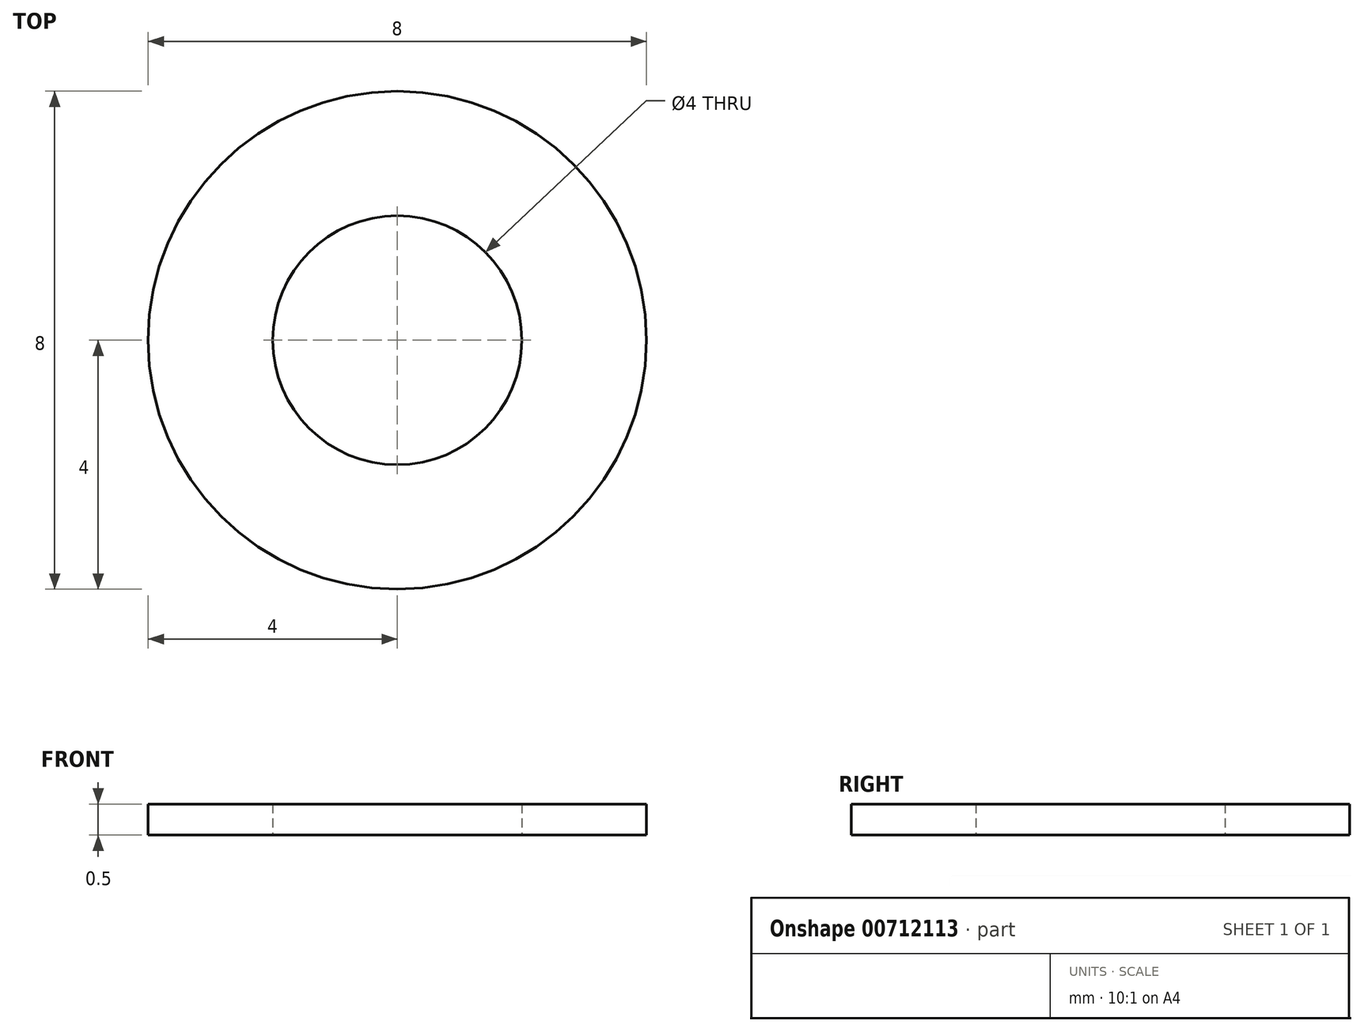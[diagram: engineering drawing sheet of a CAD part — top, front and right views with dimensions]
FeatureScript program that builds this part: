
annotation { "Feature Type Name" : "Feature", "Feature Type Description" : "" }
export const myFeature = defineFeature(function(context is Context, id is Id, definition is map)
    precondition{}
    {
        {
            var Q0;
            Q0=qCreatedBy(makeId("Top.planeOp"),FACE);
            var sketch = newSketch(context, id + "F0", { "sketchPlane" : qUnion([Q0])});
            skCircle(sketch, "E0", {"center": v(0, 0) * mm, "radius": 4 * mm});
            skCircle(sketch, "E1", {"center": v(0, 0) * mm, "radius": 2 * mm});
            skSolve(sketch);
        }
        {
            var Q0;
            Q0=makeQuery(id+"F0.imprint","IMPRINT",FACE,{"disambiguationData":[TD([[makeQuery(id+"F0.imprint","IMPRINT",EDGE,{"derivedFrom":sQuery(id+"F0.wireOp",EDGE,"E0")}),1.0]])]});
            extrude(context, id + "F1", {"entities" : qUnion([Q0]), "depth" : .5 * mm, "offsetDistance" : 25 * mm});
        }
    });
